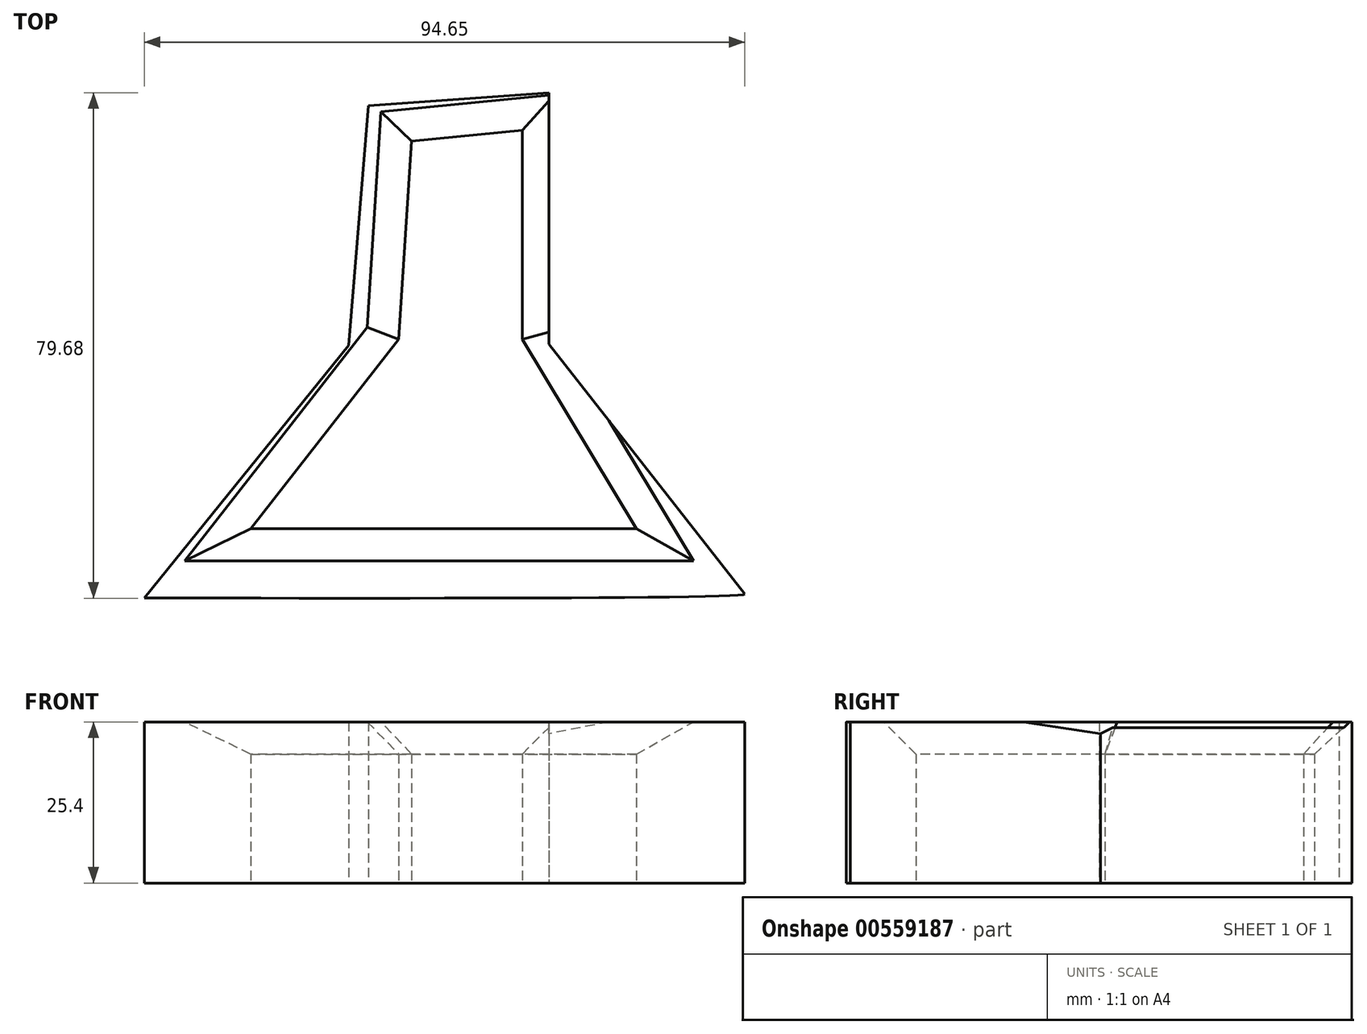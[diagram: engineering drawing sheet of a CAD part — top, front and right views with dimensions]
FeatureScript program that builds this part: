
annotation { "Feature Type Name" : "Feature", "Feature Type Description" : "" }
export const myFeature = defineFeature(function(context is Context, id is Id, definition is map)
    precondition{}
    {
        {
            var Q0;
            Q0=qCreatedBy(makeId("Top.planeOp"),FACE);
            var sketch = newSketch(context, id + "F0", { "sketchPlane" : qUnion([Q0])});
            skFitSpline(sketch, "E0", {"points": [v(-48.32, -59.75) * mm, v(46.33, -59.12) * mm, v(44.95, -58.83) * mm], "startDerivative": vector(159.2, -0.15) * mm, "endDerivative": vector(-19.18, 2.74) * mm});
            skFitSpline(sketch, "E1", {"points": [v(220.46, -4.72) * mm, v(218.88, 0) * mm], "startDerivative": vector(-1.58, 4.72) * mm, "endDerivative": vector(-1.58, 4.72) * mm});
            skFitSpline(sketch, "E2", {"points": [v(46.33, -59.12) * mm, v(0, 0) * mm], "startDerivative": vector(-46.33, 59.12) * mm, "endDerivative": vector(-46.33, 59.12) * mm});
            skFitSpline(sketch, "E3", {"points": [v(-48.32, -59.75) * mm, v(0, 0) * mm], "startDerivative": vector(48.32, 59.75) * mm, "endDerivative": vector(48.32, 59.75) * mm});
            skFitSpline(sketch, "E4", {"points": [v(15.44, -19.7) * mm, v(15.44, 19.91) * mm], "startDerivative": vector(0, 39.62) * mm, "endDerivative": vector(0, 39.62) * mm});
            skFitSpline(sketch, "E5", {"points": [v(-16.1, -19.92) * mm, v(-13, 17.9) * mm], "startDerivative": vector(3.1, 37.8) * mm, "endDerivative": vector(3.1, 37.8) * mm});
            skFitSpline(sketch, "E6", {"points": [v(15.44, 19.91) * mm, v(-13, 17.9) * mm], "startDerivative": vector(-28.45, -2.02) * mm, "endDerivative": vector(-28.45, -2.02) * mm});
            skSolve(sketch);
        }
        {
            var Q0;
            {var subQ0=sQuery(id+"F0.wireOp",EDGE,"E3");var subQ4=sQuery(id+"F0.wireOp",EDGE,"E0");var subQ7=makeQuery(id+"F0.imprint","INTERSECT",VERTEX,{"derivedFrom":[subQ4,subQ0]});Q0=makeQuery(id+"F0.imprint","IMPRINT",FACE,{"disambiguationData":[TD([[makeQuery(id+"F0.imprint","IMPRINT",EDGE,{"disambiguationData":[TD([[subQ7,-1.0]])],"derivedFrom":subQ4}),1.0]])]});}
            var Q1;
            {var subQ1=sQuery(id+"F0.wireOp",EDGE,"E4");Q1=makeQuery(id+"F0.imprint","IMPRINT",FACE,{"disambiguationData":[TD([[makeQuery(id+"F0.imprint","IMPRINT",EDGE,{"derivedFrom":subQ1}),1.0]])]});}
            extrude(context, id + "F1", {"entities" : qUnion([Q0, Q1]), "depth" : 25.4 * mm, "offsetDistance" : 25.4 * mm});
        }
        {
            var Q0;
            Q0=qCreatedBy(makeId("Top.planeOp"),FACE);
            var sketch = newSketch(context, id + "F2", { "sketchPlane" : qUnion([Q0])});
            skFitSpline(sketch, "E7", {"points": [v(-6.2, 12.28) * mm, v(-8.2, -18.98) * mm], "startDerivative": vector(-2, -31.26) * mm, "endDerivative": vector(-2, -31.26) * mm});
            skFitSpline(sketch, "E8", {"points": [v(-8.2, -18.98) * mm, v(-31.54, -48.81) * mm], "startDerivative": vector(-23.34, -29.83) * mm, "endDerivative": vector(-23.34, -29.83) * mm});
            skFitSpline(sketch, "E9", {"points": [v(-31.54, -48.81) * mm, v(20.42, -48.81) * mm], "startDerivative": vector(51.96, 0) * mm, "endDerivative": vector(51.96, 0) * mm});
            skFitSpline(sketch, "E10", {"points": [v(20.42, -48.81) * mm, v(29.26, -48.81) * mm], "startDerivative": vector(8.84, 0) * mm, "endDerivative": vector(8.84, 0) * mm});
            skFitSpline(sketch, "E11", {"points": [v(29.26, -48.81) * mm, v(11.25, -18.98) * mm], "startDerivative": vector(-18, 29.83) * mm, "endDerivative": vector(-18, 29.83) * mm});
            skFitSpline(sketch, "E12", {"points": [v(11.25, -18.98) * mm, v(11.25, 14) * mm], "startDerivative": vector(0, 32.98) * mm, "endDerivative": vector(0, 32.98) * mm});
            skFitSpline(sketch, "E13", {"points": [v(11.25, 14) * mm, v(-6.2, 12.28) * mm], "startDerivative": vector(-17.45, -1.72) * mm, "endDerivative": vector(-17.45, -1.72) * mm});
            skSolve(sketch);
        }
        {
            var Q0;
            Q0=makeQuery(id+"F2.imprint","IMPRINT",FACE,{"disambiguationData":[TD([[makeQuery(id+"F2.imprint","IMPRINT",EDGE,{"derivedFrom":sQuery(id+"F2.wireOp",EDGE,"E7")}),1.0]])]});
            extrude(context, id + "F3", {"entities" : qUnion([Q0]), "operationType" : NewBodyOperationType.REMOVE, "depth" : 50.8 * mm, "offsetDistance" : 25.4 * mm});
        }
        {
            var Q0;
            Q0=makeQuery(id+"F3.boolean.opBoolean","INTERSECT",EDGE,{"derivedFrom":[makeQuery(id+"F1.opExtrude","CAP_FACE",FACE,{"disambiguationData":[OSD([sQuery(id+"F0.wireOp",EDGE,"E0"),sQuery(id+"F0.wireOp",EDGE,"E2"),sQuery(id+"F0.wireOp",EDGE,"E3"),sQuery(id+"F0.wireOp",EDGE,"E4"),sQuery(id+"F0.wireOp",EDGE,"E5"),sQuery(id+"F0.wireOp",EDGE,"E6")])],"isStart":false}),makeQuery(id+"F3.opExtrude","SWEPT_FACE",FACE,{"disambiguationData":[OSD([sQuery(id+"F2.wireOp",EDGE,"E7")])]})]});
            var Q1;
            Q1=makeQuery(id+"F3.boolean.opBoolean","INTERSECT",EDGE,{"derivedFrom":[makeQuery(id+"F1.opExtrude","CAP_FACE",FACE,{"disambiguationData":[OSD([sQuery(id+"F0.wireOp",EDGE,"E0"),sQuery(id+"F0.wireOp",EDGE,"E2"),sQuery(id+"F0.wireOp",EDGE,"E3"),sQuery(id+"F0.wireOp",EDGE,"E4"),sQuery(id+"F0.wireOp",EDGE,"E5"),sQuery(id+"F0.wireOp",EDGE,"E6")])],"isStart":false}),makeQuery(id+"F3.opExtrude","SWEPT_FACE",FACE,{"disambiguationData":[OSD([sQuery(id+"F2.wireOp",EDGE,"E13")])]})]});
            chamfer(context, id + "F4", {"entities" : qUnion([Q0, Q1]), "width" : 5.08 * mm, "tangentPropagation" : true});
        }
        {
            var Q0;
            Q0=makeQuery(id+"F3.boolean.opBoolean","INTERSECT",EDGE,{"derivedFrom":[makeQuery(id+"F1.opExtrude","CAP_FACE",FACE,{"disambiguationData":[OSD([sQuery(id+"F0.wireOp",EDGE,"E0"),sQuery(id+"F0.wireOp",EDGE,"E2"),sQuery(id+"F0.wireOp",EDGE,"E3"),sQuery(id+"F0.wireOp",EDGE,"E4"),sQuery(id+"F0.wireOp",EDGE,"E5"),sQuery(id+"F0.wireOp",EDGE,"E6")])],"isStart":false}),makeQuery(id+"F3.opExtrude","SWEPT_FACE",FACE,{"disambiguationData":[OSD([sQuery(id+"F2.wireOp",EDGE,"E8")])]})]});
            var Q1;
            Q1=makeQuery(id+"F3.boolean.opBoolean","INTERSECT",EDGE,{"derivedFrom":[makeQuery(id+"F1.opExtrude","CAP_FACE",FACE,{"disambiguationData":[OSD([sQuery(id+"F0.wireOp",EDGE,"E0"),sQuery(id+"F0.wireOp",EDGE,"E2"),sQuery(id+"F0.wireOp",EDGE,"E3"),sQuery(id+"F0.wireOp",EDGE,"E4"),sQuery(id+"F0.wireOp",EDGE,"E5"),sQuery(id+"F0.wireOp",EDGE,"E6")])],"isStart":false}),makeQuery(id+"F3.opExtrude","SWEPT_FACE",FACE,{"disambiguationData":[OSD([sQuery(id+"F2.wireOp",EDGE,"E9")])]})]});
            var Q2;
            Q2=makeQuery(id+"F3.boolean.opBoolean","INTERSECT",EDGE,{"derivedFrom":[makeQuery(id+"F1.opExtrude","CAP_FACE",FACE,{"disambiguationData":[OSD([sQuery(id+"F0.wireOp",EDGE,"E0"),sQuery(id+"F0.wireOp",EDGE,"E2"),sQuery(id+"F0.wireOp",EDGE,"E3"),sQuery(id+"F0.wireOp",EDGE,"E4"),sQuery(id+"F0.wireOp",EDGE,"E5"),sQuery(id+"F0.wireOp",EDGE,"E6")])],"isStart":false}),makeQuery(id+"F3.opExtrude","SWEPT_FACE",FACE,{"disambiguationData":[OSD([sQuery(id+"F2.wireOp",EDGE,"E11")])]})]});
            var Q3;
            Q3=makeQuery(id+"F3.boolean.opBoolean","INTERSECT",EDGE,{"derivedFrom":[makeQuery(id+"F1.opExtrude","CAP_FACE",FACE,{"disambiguationData":[OSD([sQuery(id+"F0.wireOp",EDGE,"E0"),sQuery(id+"F0.wireOp",EDGE,"E2"),sQuery(id+"F0.wireOp",EDGE,"E3"),sQuery(id+"F0.wireOp",EDGE,"E4"),sQuery(id+"F0.wireOp",EDGE,"E5"),sQuery(id+"F0.wireOp",EDGE,"E6")])],"isStart":false}),makeQuery(id+"F3.opExtrude","SWEPT_FACE",FACE,{"disambiguationData":[OSD([sQuery(id+"F2.wireOp",EDGE,"E10")])]})]});
            var Q4;
            Q4=makeQuery(id+"F3.boolean.opBoolean","INTERSECT",EDGE,{"derivedFrom":[makeQuery(id+"F1.opExtrude","CAP_FACE",FACE,{"disambiguationData":[OSD([sQuery(id+"F0.wireOp",EDGE,"E0"),sQuery(id+"F0.wireOp",EDGE,"E2"),sQuery(id+"F0.wireOp",EDGE,"E3"),sQuery(id+"F0.wireOp",EDGE,"E4"),sQuery(id+"F0.wireOp",EDGE,"E5"),sQuery(id+"F0.wireOp",EDGE,"E6")])],"isStart":false}),makeQuery(id+"F3.opExtrude","SWEPT_FACE",FACE,{"disambiguationData":[OSD([sQuery(id+"F2.wireOp",EDGE,"E12")])]})]});
            chamfer(context, id + "F5", {"entities" : qUnion([Q0, Q1, Q2, Q3, Q4]), "width" : 5.08 * mm, "tangentPropagation" : true});
        }
    });
